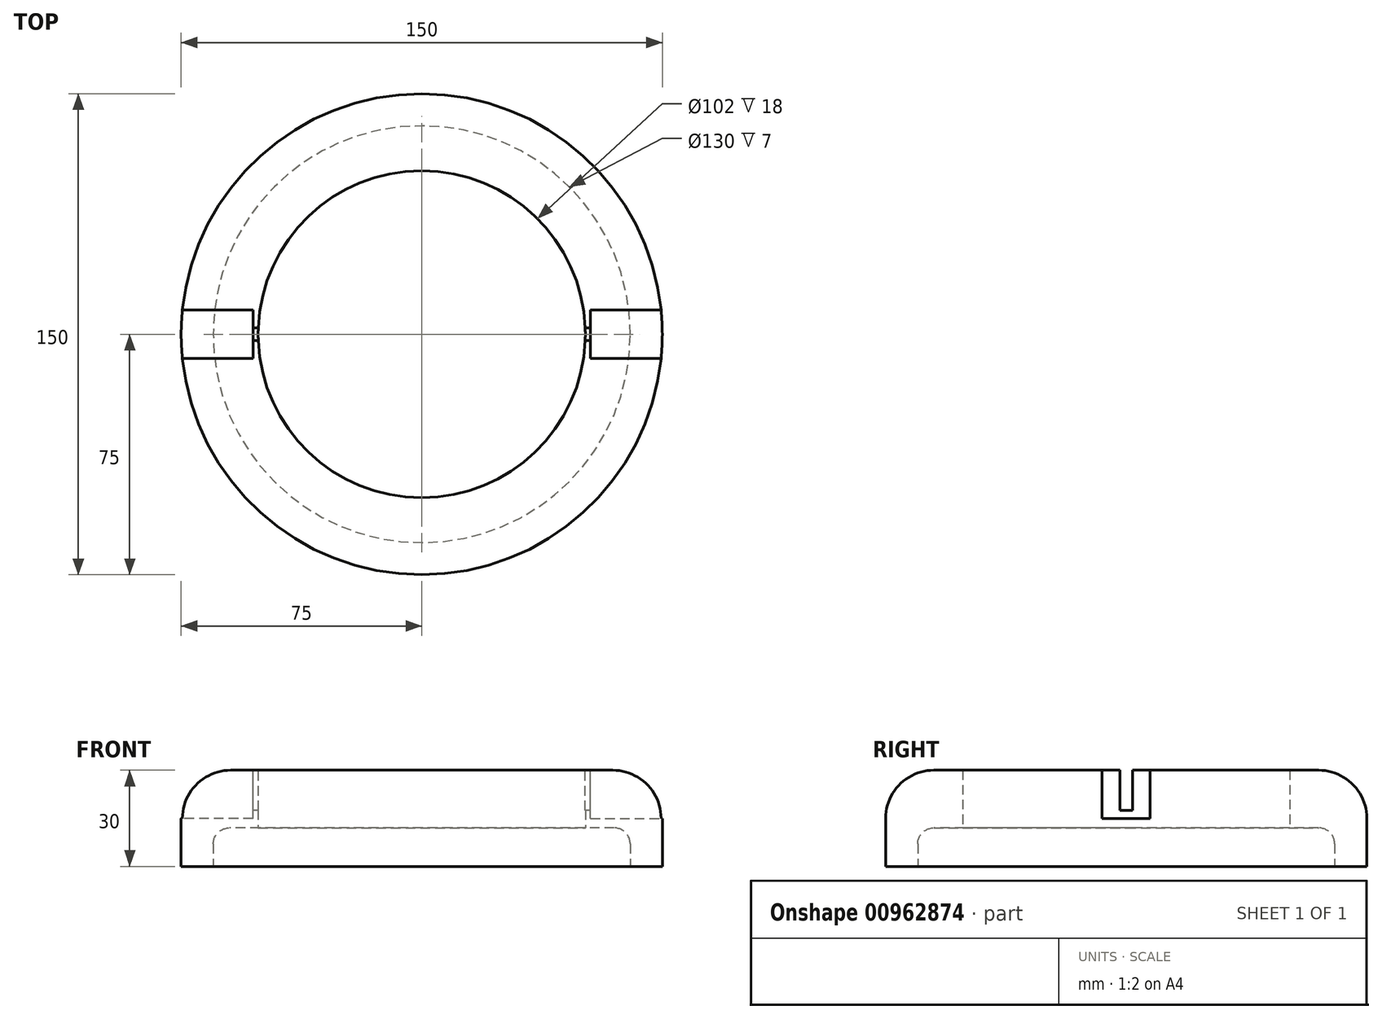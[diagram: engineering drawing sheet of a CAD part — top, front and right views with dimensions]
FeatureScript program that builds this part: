
annotation { "Feature Type Name" : "Feature", "Feature Type Description" : "" }
export const myFeature = defineFeature(function(context is Context, id is Id, definition is map)
    precondition{}
    {
        {
            var Q0;
            Q0=qCreatedBy(makeId("Top.planeOp"),FACE);
            var sketch = newSketch(context, id + "F0", { "sketchPlane" : qUnion([Q0])});
            skCircle(sketch, "E0", {"center": v(0, 0) * mm, "radius": 51 * mm});
            skCircle(sketch, "E1", {"center": v(0, 0) * mm, "radius": 75 * mm});
            skCircle(sketch, "E2.0", {"center": v(0, 0) * mm, "radius": 65 * mm});
            skSolve(sketch);
        }
        {
            var Q0;
            Q0=makeQuery(id+"F0.imprint","IMPRINT",FACE,{"disambiguationData":[TD([[makeQuery(id+"F0.imprint","IMPRINT",EDGE,{"derivedFrom":sQuery(id+"F0.wireOp",EDGE,"E0")}),-1.0]])]});
            var Q1;
            Q1=makeQuery(id+"F0.imprint","IMPRINT",FACE,{"disambiguationData":[TD([[makeQuery(id+"F0.imprint","IMPRINT",EDGE,{"derivedFrom":sQuery(id+"F0.wireOp",EDGE,"E1")}),1.0]])]});
            extrude(context, id + "F1", {"entities" : qUnion([Q0, Q1]), "depth" : 30 * mm, "offsetDistance" : 25 * mm});
        }
        {
            var Q0;
            Q0=makeQuery(id+"F1.opExtrude","CAP_FACE",FACE,{"disambiguationData":[OSD([sQuery(id+"F0.wireOp",EDGE,"E0"),sQuery(id+"F0.wireOp",EDGE,"E1")])],"isStart":false});
            var sketch = newSketch(context, id + "F2", { "sketchPlane" : qUnion([Q0])});
            skLineSegment(sketch, "E3.bottom", {"start": v(75, -2) * mm, "end": v(-75, -2) * mm});
            skLineSegment(sketch, "E3.top", {"start": v(75, 2) * mm, "end": v(-75, 2) * mm});
            skLineSegment(sketch, "E3.left", {"start": v(75, -2) * mm, "end": v(75, 2) * mm});
            skLineSegment(sketch, "E3.right", {"start": v(-75, -2) * mm, "end": v(-75, 2) * mm});
            skPoint(sketch, "E3.middle", {"position": v(0, 0) * mm});
            skLineSegment(sketch, "E4.bottom", {"start": v(-52.6, -7.5) * mm, "end": v(-97.4, -7.5) * mm});
            skLineSegment(sketch, "E4.top", {"start": v(-52.6, 7.5) * mm, "end": v(-97.4, 7.5) * mm});
            skLineSegment(sketch, "E4.left", {"start": v(-52.6, -7.5) * mm, "end": v(-52.6, 7.5) * mm});
            skLineSegment(sketch, "E4.right", {"start": v(-97.4, -7.5) * mm, "end": v(-97.4, 7.5) * mm});
            skPoint(sketch, "E4.middle", {"position": v(-75, 0) * mm});
            skLineSegment(sketch, "E5", {"start": v(0, 0) * mm, "end": v(0, 75) * mm, "construction": true});
            skLineSegment(sketch, "E6.MirrorCS", {"start": v(52.6, 7.5) * mm, "end": v(97.4, 7.5) * mm});
            skLineSegment(sketch, "E7.MirrorCS", {"start": v(97.4, -7.5) * mm, "end": v(97.4, 7.5) * mm});
            skLineSegment(sketch, "E8.MirrorCS", {"start": v(52.6, -7.5) * mm, "end": v(52.6, 7.5) * mm});
            skLineSegment(sketch, "E9.MirrorCS", {"start": v(52.6, -7.5) * mm, "end": v(97.4, -7.5) * mm});
            skSolve(sketch);
        }
        {
            var Q0;
            Q0=makeQuery(id+"F0.imprint","IMPRINT",FACE,{"disambiguationData":[TD([[makeQuery(id+"F0.imprint","IMPRINT",EDGE,{"derivedFrom":sQuery(id+"F0.wireOp",EDGE,"E0")}),-1.0]])]});
            extrude(context, id + "F3", {"entities" : qUnion([Q0]), "operationType" : NewBodyOperationType.REMOVE, "depth" : 12 * mm, "offsetDistance" : 25 * mm});
        }
        {
            var Q0;
            Q0=makeQuery(id+"F3.boolean.opBoolean","COPY",EDGE,{"derivedFrom":makeQuery(id+"F3.opExtrude","CAP_EDGE",EDGE,{"disambiguationData":[OSD([sQuery(id+"F0.wireOp",EDGE,"E2.0")])],"isStart":false})});
            fillet(context, id + "F4", {"entities" : qUnion([Q0]), "radius" : 5 * mm, "tangentPropagation" : true, "allowEdgeOverflow" : false});
        }
        {
            var Q0;
            Q0=makeQuery(id+"F1.opExtrude","CAP_EDGE",EDGE,{"disambiguationData":[OSD([sQuery(id+"F0.wireOp",EDGE,"E1")])],"isStart":false});
            fillet(context, id + "F5", {"entities" : qUnion([Q0]), "radius" : 15 * mm, "tangentPropagation" : true, "allowEdgeOverflow" : false});
        }
        {
            var Q0;
            {var subQ0=sQuery(id+"F2.wireOp",EDGE,"E3.bottom");var subQ4=sQuery(id+"F2.wireOp",EDGE,"E8.MirrorCS");var subQ5=makeQuery(id+"F2.imprint","INTERSECT",VERTEX,{"derivedFrom":[subQ0,subQ4]});Q0=makeQuery(id+"F2.imprint","IMPRINT",FACE,{"disambiguationData":[TD([[makeQuery(id+"F2.imprint","IMPRINT",EDGE,{"disambiguationData":[TD([[subQ5,1.0]])],"derivedFrom":subQ0}),-1.0]])]});}
            var Q1;
            {var subQ0=sQuery(id+"F2.wireOp",EDGE,"E8.MirrorCS");var subQ1=sQuery(id+"F2.wireOp",EDGE,"E3.top");var subQ2=makeQuery(id+"F2.imprint","INTERSECT",VERTEX,{"derivedFrom":[subQ1,subQ0]});Q1=makeQuery(id+"F2.imprint","IMPRINT",FACE,{"disambiguationData":[TD([[makeQuery(id+"F2.imprint","IMPRINT",EDGE,{"disambiguationData":[TD([[subQ2,1.0]])],"derivedFrom":subQ1}),-1.0]])]});}
            var Q2;
            {var subQ0=sQuery(id+"F2.wireOp",EDGE,"E8.MirrorCS");var subQ1=sQuery(id+"F2.wireOp",EDGE,"E3.bottom");var subQ2=makeQuery(id+"F2.imprint","INTERSECT",VERTEX,{"derivedFrom":[subQ1,subQ0]});Q2=makeQuery(id+"F2.imprint","IMPRINT",FACE,{"disambiguationData":[TD([[makeQuery(id+"F2.imprint","IMPRINT",EDGE,{"disambiguationData":[TD([[subQ2,1.0]])],"derivedFrom":subQ1}),1.0]])]});}
            var Q3;
            {var subQ0=sQuery(id+"F2.wireOp",EDGE,"E4.left");var subQ1=sQuery(id+"F2.wireOp",EDGE,"E3.top");var subQ2=makeQuery(id+"F2.imprint","INTERSECT",VERTEX,{"derivedFrom":[subQ1,subQ0]});Q3=makeQuery(id+"F2.imprint","IMPRINT",FACE,{"disambiguationData":[TD([[makeQuery(id+"F2.imprint","IMPRINT",EDGE,{"disambiguationData":[TD([[subQ2,-1.0]])],"derivedFrom":subQ1}),-1.0]])]});}
            var Q4;
            {var subQ0=sQuery(id+"F2.wireOp",EDGE,"E4.left");var subQ1=sQuery(id+"F2.wireOp",EDGE,"E3.bottom");var subQ2=makeQuery(id+"F2.imprint","INTERSECT",VERTEX,{"derivedFrom":[subQ1,subQ0]});Q4=makeQuery(id+"F2.imprint","IMPRINT",FACE,{"disambiguationData":[TD([[makeQuery(id+"F2.imprint","IMPRINT",EDGE,{"disambiguationData":[TD([[subQ2,-1.0]])],"derivedFrom":subQ1}),-1.0]])]});}
            var Q5;
            {var subQ0=sQuery(id+"F2.wireOp",EDGE,"E4.left");var subQ1=sQuery(id+"F2.wireOp",EDGE,"E3.bottom");var subQ2=makeQuery(id+"F2.imprint","INTERSECT",VERTEX,{"derivedFrom":[subQ1,subQ0]});Q5=makeQuery(id+"F2.imprint","IMPRINT",FACE,{"disambiguationData":[TD([[makeQuery(id+"F2.imprint","IMPRINT",EDGE,{"disambiguationData":[TD([[subQ2,-1.0]])],"derivedFrom":subQ1}),1.0]])]});}
            extrude(context, id + "F6", {"entities" : qUnion([Q0, Q1, Q2, Q3, Q4, Q5]), "operationType" : NewBodyOperationType.REMOVE, "oppositeDirection" : true, "depth" : 15 * mm, "offsetDistance" : 25 * mm});
        }
        {
            var Q0;
            {var subQ0=sQuery(id+"F2.wireOp",EDGE,"E4.left");var subQ1=sQuery(id+"F2.wireOp",EDGE,"E3.bottom");var subQ2=makeQuery(id+"F2.imprint","INTERSECT",VERTEX,{"derivedFrom":[subQ1,subQ0]});Q0=makeQuery(id+"F2.imprint","IMPRINT",FACE,{"disambiguationData":[TD([[makeQuery(id+"F2.imprint","IMPRINT",EDGE,{"disambiguationData":[TD([[subQ2,1.0]])],"derivedFrom":subQ1}),-1.0]])]});}
            var Q1;
            {var subQ0=sQuery(id+"F2.wireOp",EDGE,"E8.MirrorCS");var subQ1=sQuery(id+"F2.wireOp",EDGE,"E3.bottom");var subQ2=makeQuery(id+"F2.imprint","INTERSECT",VERTEX,{"derivedFrom":[subQ1,subQ0]});Q1=makeQuery(id+"F2.imprint","IMPRINT",FACE,{"disambiguationData":[TD([[makeQuery(id+"F2.imprint","IMPRINT",EDGE,{"disambiguationData":[TD([[subQ2,-1.0]])],"derivedFrom":subQ1}),-1.0]])]});}
            extrude(context, id + "F7", {"entities" : qUnion([Q0, Q1]), "operationType" : NewBodyOperationType.REMOVE, "oppositeDirection" : true, "depth" : 12.5 * mm, "offsetDistance" : 25 * mm});
        }
    });
